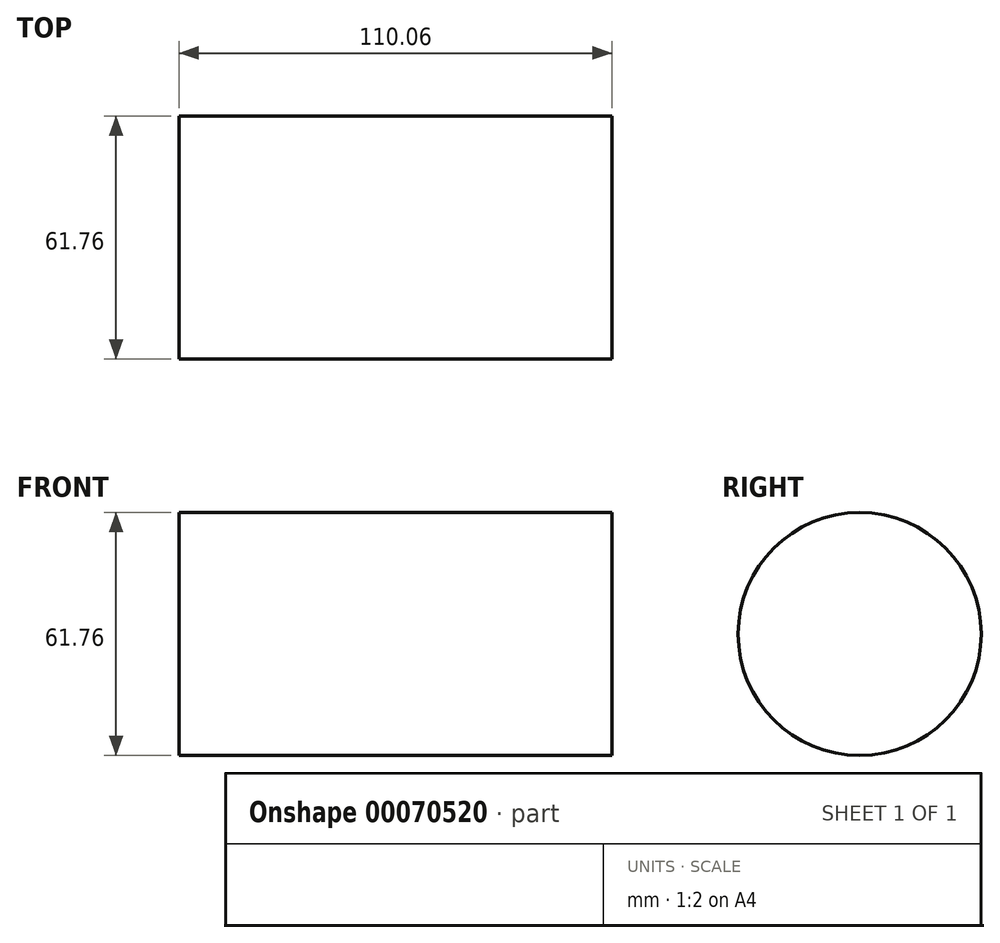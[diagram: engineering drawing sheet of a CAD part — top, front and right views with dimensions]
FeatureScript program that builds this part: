
annotation { "Feature Type Name" : "Feature", "Feature Type Description" : "" }
export const myFeature = defineFeature(function(context is Context, id is Id, definition is map)
    precondition{}
    {
        {
            var Q0;
            Q0=qCreatedBy(makeId("Right.planeOp"),FACE);
            var sketch = newSketch(context, id + "F0", { "sketchPlane" : qUnion([Q0])});
            skCircle(sketch, "E0", {"center": v(0, -0.98) * mm, "radius": 30.88 * mm});
            skSolve(sketch);
        }
        {
            var Q0;
            Q0=makeQuery(id+"F0.imprint","IMPRINT",FACE,{"disambiguationData":[TD([[makeQuery(id+"F0.imprint","IMPRINT",EDGE,{"derivedFrom":sQuery(id+"F0.wireOp",EDGE,"E0")}),1.0]])]});
            extrude(context, id + "F1", {"entities" : qUnion([Q0]), "depth" : 110.06 * mm});
        }
    });
